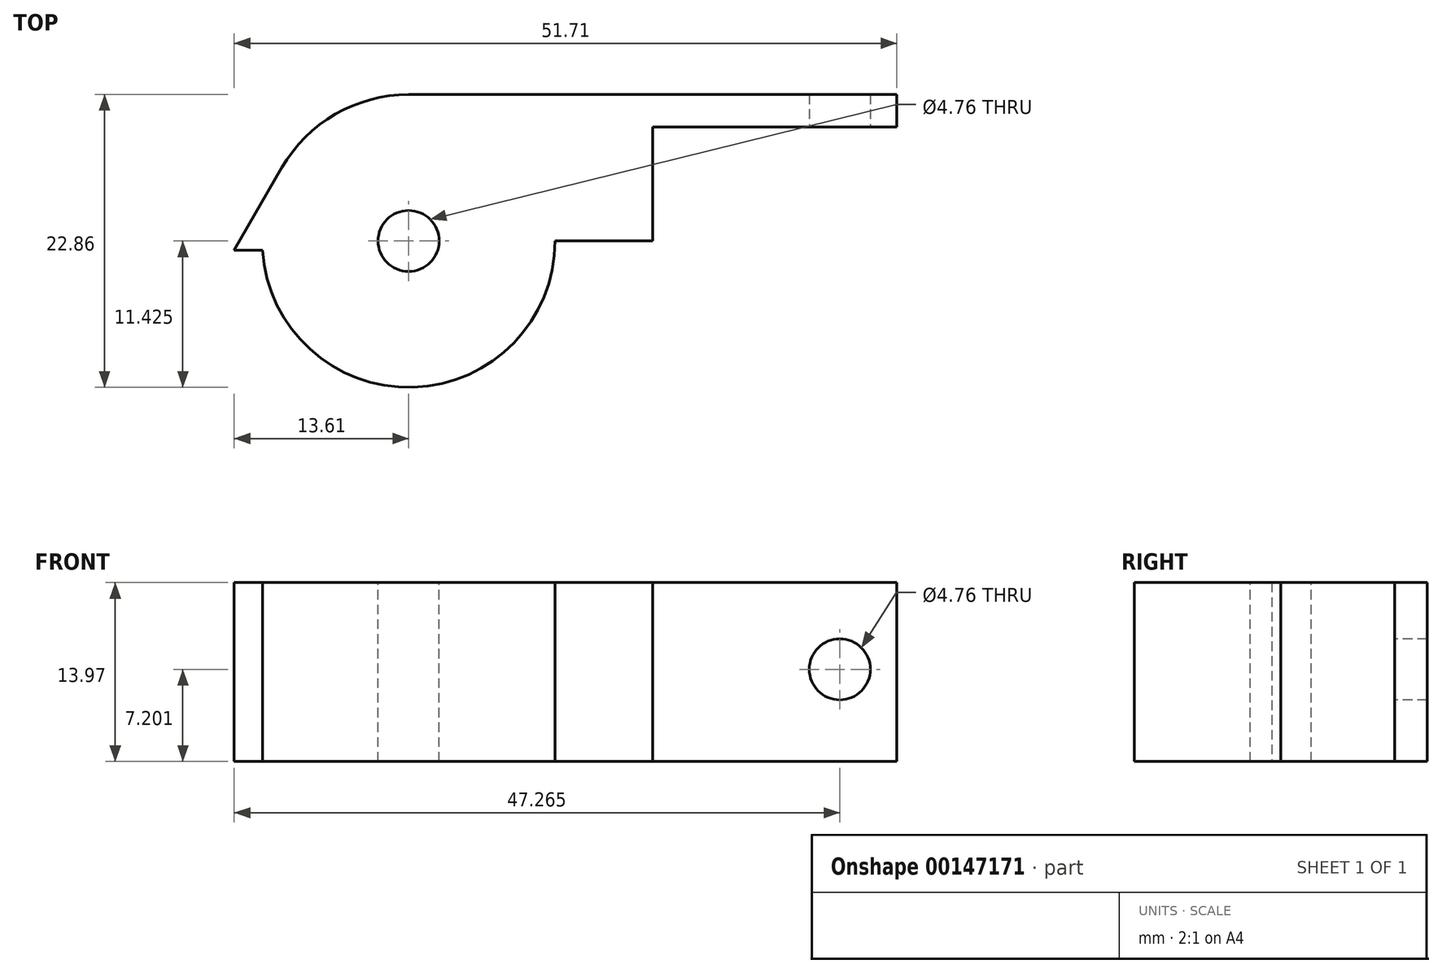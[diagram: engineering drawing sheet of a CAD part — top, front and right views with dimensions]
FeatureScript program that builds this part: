
annotation { "Feature Type Name" : "Feature", "Feature Type Description" : "" }
export const myFeature = defineFeature(function(context is Context, id is Id, definition is map)
    precondition{}
    {
        {
            var Q0;
            Q0=qCreatedBy(makeId("Top.planeOp"),FACE);
            var sketch = newSketch(context, id + "F0", { "sketchPlane" : qUnion([Q0])});
            skLineSegment(sketch, "E0.bottom", {"start": v(19.05, -5.71) * mm, "end": v(-7.62, -5.72) * mm});
            skLineSegment(sketch, "E0.top", {"start": v(19.05, 5.72) * mm, "end": v(-19.05, 5.71) * mm});
            skLineSegment(sketch, "E0.left", {"start": v(19.05, -5.71) * mm, "end": v(19.05, 5.72) * mm});
            skPoint(sketch, "E0.middle", {"position": v(0, 0) * mm});
            skCircle(sketch, "E1", {"center": v(-19.05, -5.71) * mm, "radius": 11.43 * mm});
            skLineSegment(sketch, "E2", {"start": v(-28.95, 0) * mm, "end": v(-32.66, -6.43) * mm});
            skLineSegment(sketch, "E3", {"start": v(-32.66, -6.43) * mm, "end": v(-30.46, -6.43) * mm});
            skSolve(sketch);
        }
        {
            var Q0;
            {var subQ0=sQuery(id+"F0.wireOp",EDGE,"E1");var subQ1=makeQuery(id+"F0.imprint","INTERSECT",VERTEX,{"derivedFrom":[sQuery(id+"F0.wireOp",EDGE,"E0.bottom"),subQ0]});Q0=makeQuery(id+"F0.imprint","IMPRINT",FACE,{"disambiguationData":[TD([[makeQuery(id+"F0.imprint","IMPRINT",EDGE,{"disambiguationData":[TD([[subQ1,-1.0]])],"derivedFrom":subQ0}),1.0]])]});}
            var Q1;
            {var subQ0=sQuery(id+"F0.wireOp",EDGE,"E0.bottom");Q1=makeQuery(id+"F0.imprint","IMPRINT",FACE,{"disambiguationData":[TD([[makeQuery(id+"F0.imprint","IMPRINT",EDGE,{"derivedFrom":subQ0}),-1.0]])]});}
            var Q2;
            {var subQ0=sQuery(id+"F0.wireOp",EDGE,"E2");Q2=makeQuery(id+"F0.imprint","IMPRINT",FACE,{"disambiguationData":[TD([[makeQuery(id+"F0.imprint","IMPRINT",EDGE,{"derivedFrom":subQ0}),1.0]])]});}
            extrude(context, id + "F1", {"entities" : qUnion([Q0, Q1, Q2]), "depth" : 13.97 * mm});
        }
        {
            var Q0;
            Q0=makeQuery(id+"F1.opExtrude","CAP_FACE",FACE,{"disambiguationData":[OSD([sQuery(id+"F0.wireOp",EDGE,"E0.bottom"),sQuery(id+"F0.wireOp",EDGE,"E0.top"),sQuery(id+"F0.wireOp",EDGE,"E0.left"),sQuery(id+"F0.wireOp",EDGE,"E1"),sQuery(id+"F0.wireOp",EDGE,"E2"),sQuery(id+"F0.wireOp",EDGE,"E3")])],"isStart":false});
            var sketch = newSketch(context, id + "F2", { "sketchPlane" : qUnion([Q0])});
            skPoint(sketch, "E4", {"position": v(-19.05, -5.71) * mm});
            skSolve(sketch);
        }
        {
            var Q0;
            Q0=sQuery(id+"F2.wireOp",VERTEX,"E4");
            var Q1;
            Q1=makeQuery(id+"F1.opExtrude","SWEPT_BODY",BODY,{"disambiguationData":[OSD([sQuery(id+"F0.wireOp",EDGE,"E0.bottom"),sQuery(id+"F0.wireOp",EDGE,"E0.top"),sQuery(id+"F0.wireOp",EDGE,"E0.left"),sQuery(id+"F0.wireOp",EDGE,"E1"),sQuery(id+"F0.wireOp",EDGE,"E2"),sQuery(id+"F0.wireOp",EDGE,"E3")])]});
            hole(context, id + "F3", {"style" : HoleStyle.SIMPLE, "endStyle" : HoleEndStyle.THROUGH, "holeDiameter" : 4.76 * mm, "locations" : qUnion([Q0]), "scope" : qUnion([Q1]), "isTappedThrough" : true});
        }
        {
            var Q0;
            Q0=makeQuery(id+"F1.opExtrude","SWEPT_FACE",FACE,{"disambiguationData":[OSD([sQuery(id+"F0.wireOp",EDGE,"E0.bottom")])]});
            var sketch = newSketch(context, id + "F4", { "sketchPlane" : qUnion([Q0])});
            skLineSegment(sketch, "E5.bottom", {"start": v(19.05, 13.97) * mm, "end": v(0, 13.97) * mm});
            skLineSegment(sketch, "E5.top", {"start": v(19.05, 0) * mm, "end": v(0, 0) * mm});
            skLineSegment(sketch, "E5.left", {"start": v(19.05, 13.97) * mm, "end": v(19.05, 0) * mm});
            skLineSegment(sketch, "E5.right", {"start": v(0, 13.97) * mm, "end": v(0, 0) * mm});
            skSolve(sketch);
        }
        {
            var Q0;
            Q0=makeQuery(id+"F4.imprint","IMPRINT",FACE,{"disambiguationData":[TD([[makeQuery(id+"F4.imprint","IMPRINT",EDGE,{"derivedFrom":sQuery(id+"F4.wireOp",EDGE,"E5.bottom")}),1.0]])]});
            extrude(context, id + "F5", {"entities" : qUnion([Q0]), "operationType" : NewBodyOperationType.REMOVE, "oppositeDirection" : true, "depth" : 8.9 * mm});
        }
        {
            var Q0;
            Q0=makeQuery(id+"F5.boolean.opBoolean","COPY",FACE,{"derivedFrom":makeQuery(id+"F5.opExtrude","CAP_FACE",FACE,{"disambiguationData":[OSD([sQuery(id+"F4.wireOp",EDGE,"E5.bottom"),sQuery(id+"F4.wireOp",EDGE,"E5.top"),sQuery(id+"F4.wireOp",EDGE,"E5.left"),sQuery(id+"F4.wireOp",EDGE,"E5.right")])],"isStart":false})});
            var sketch = newSketch(context, id + "F6", { "sketchPlane" : qUnion([Q0])});
            skPoint(sketch, "E6", {"position": v(14.6, 7.2) * mm});
            skSolve(sketch);
        }
        {
            var Q0;
            Q0=sQuery(id+"F6.wireOp",VERTEX,"E6");
            var Q1;
            Q1=makeQuery(id+"F1.opExtrude","SWEPT_BODY",BODY,{"disambiguationData":[OSD([sQuery(id+"F0.wireOp",EDGE,"E0.bottom"),sQuery(id+"F0.wireOp",EDGE,"E0.top"),sQuery(id+"F0.wireOp",EDGE,"E0.left"),sQuery(id+"F0.wireOp",EDGE,"E1"),sQuery(id+"F0.wireOp",EDGE,"E2"),sQuery(id+"F0.wireOp",EDGE,"E3")])]});
            hole(context, id + "F7", {"style" : HoleStyle.SIMPLE, "endStyle" : HoleEndStyle.THROUGH, "holeDiameter" : 4.76 * mm, "locations" : qUnion([Q0]), "scope" : qUnion([Q1]), "isTappedThrough" : true});
        }
    });
